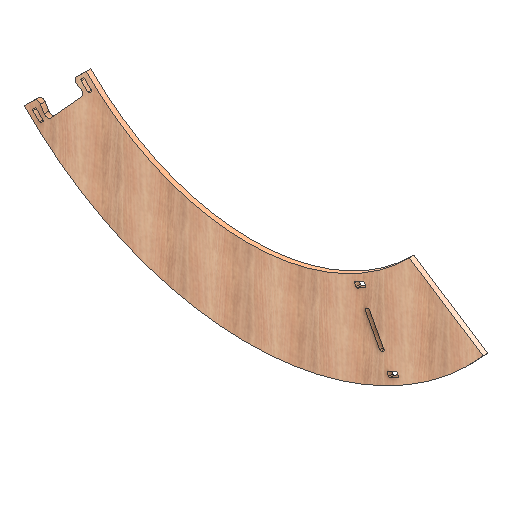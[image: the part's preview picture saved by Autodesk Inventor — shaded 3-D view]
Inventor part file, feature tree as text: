
AUTODESK INVENTOR PART (.ipt)
format: ipt  version: 2021 (Build 250183000, 183)  size: 259,584 bytes
history: native  units: mm
features: other x2, extrude x2, hole x1
ambient origin geometry x8: Origin, YZ Plane, XZ Plane, XY Plane, X Axis, Y Axis, Z Axis, Center Point
bodies: Solid1 (feature_tree)
feature tree (5):
  other  "CONTOURS"
  hole  "HOLES"  [1 undecoded]
  other  "LETTERS"
  extrude  "Extrusion1"  Depth=18.0mm TaperAngle=0.0deg
  extrude  "Extrusion2"  [1 undecoded]
note: 2 required parameter values undecoded (feature->parameter linkage not recoverable at this tier; creation-order binding heuristic only, values carry confidence <= 0.55)
